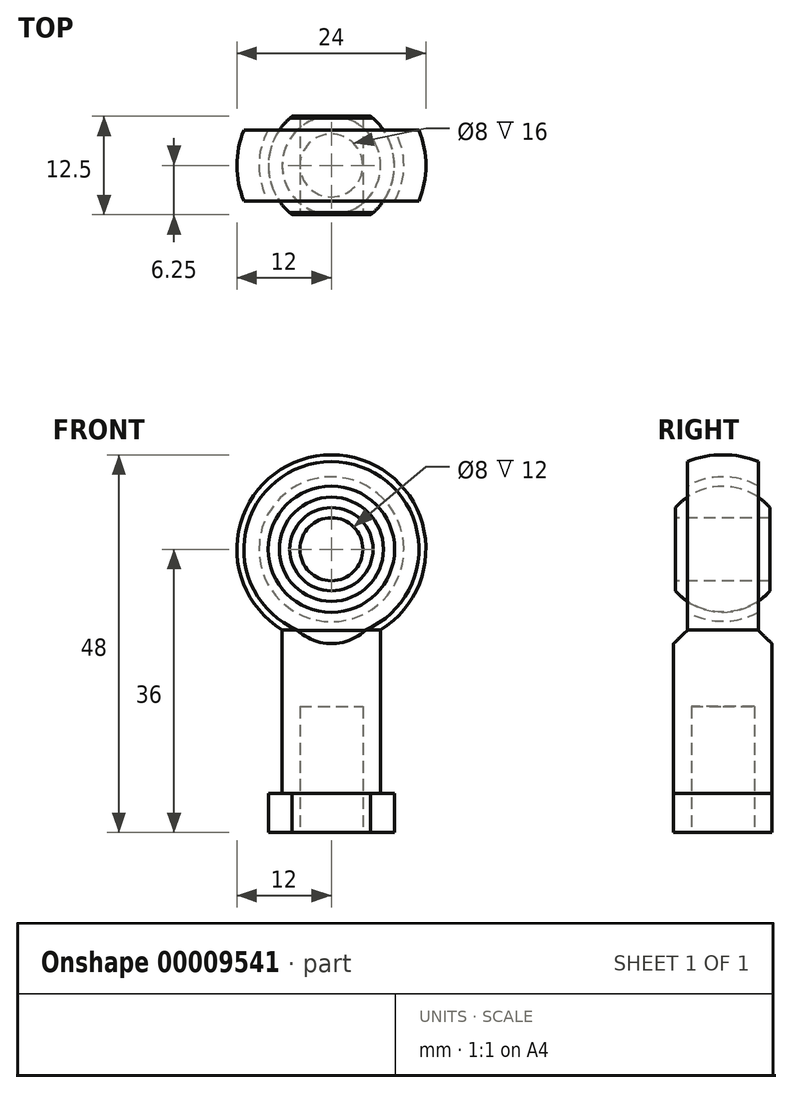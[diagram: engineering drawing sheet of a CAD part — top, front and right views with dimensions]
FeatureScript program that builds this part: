
annotation { "Feature Type Name" : "Feature", "Feature Type Description" : "" }
export const myFeature = defineFeature(function(context is Context, id is Id, definition is map)
    precondition{}
    {
        {
            var Q0;
            Q0=qCreatedBy(makeId("Front.planeOp"),FACE);
            var sketch = newSketch(context, id + "F0", { "sketchPlane" : qUnion([Q0])});
            skLineSegment(sketch, "E0", {"start": v(0, -62.5) * mm, "end": v(0, 62.8) * mm, "construction": true});
            skLineSegment(sketch, "E1", {"start": v(-34.6, 0) * mm, "end": v(39.27, 0) * mm, "construction": true});
            skLineSegment(sketch, "E2", {"start": v(0, -36) * mm, "end": v(6.25, -36) * mm});
            skCircle(sketch, "E3", {"center": v(0, 0) * mm, "radius": 12 * mm});
            skLineSegment(sketch, "E4", {"start": v(6.25, -36) * mm, "end": v(6.25, -10.24) * mm});
            skLineSegment(sketch, "E5.0", {"start": v(8, -36) * mm, "end": v(8, -31) * mm});
            skLineSegment(sketch, "E6", {"start": v(6.25, -36) * mm, "end": v(8, -36) * mm});
            skLineSegment(sketch, "E7.0", {"start": v(6.25, -31) * mm, "end": v(8, -31) * mm});
            skLineSegment(sketch, "E8", {"start": v(4, -36) * mm, "end": v(4, -20) * mm});
            skLineSegment(sketch, "E9", {"start": v(4, -20) * mm, "end": v(0, -20) * mm});
            skCircle(sketch, "E10", {"center": v(0, 0) * mm, "radius": 4 * mm});
            skCircle(sketch, "E11.0", {"center": v(0, 0) * mm, "radius": 6 * mm});
            skLineSegment(sketch, "E12", {"start": v(6.25, -10.24) * mm, "end": v(0, -10.24) * mm});
            skLineSegment(sketch, "E13", {"start": v(0, -10.24) * mm, "end": v(0, -20) * mm});
            skLineSegment(sketch, "E14.left", {"start": v(6.25, -36) * mm, "end": v(6.25, -31) * mm});
            skLineSegment(sketch, "E15.0.MirrorCS", {"start": v(-6.25, -31) * mm, "end": v(-8, -31) * mm});
            skLineSegment(sketch, "E16.0.MirrorCS", {"start": v(-8, -36) * mm, "end": v(-8, -31) * mm});
            skLineSegment(sketch, "E17.0.MirrorCS", {"start": v(-6.25, -36) * mm, "end": v(-6.25, -10.24) * mm});
            skLineSegment(sketch, "E18.0.MirrorCS", {"start": v(-6.25, -36) * mm, "end": v(-8, -36) * mm});
            skLineSegment(sketch, "E19.0.MirrorCS", {"start": v(-4, -36) * mm, "end": v(-4, -20) * mm});
            skLineSegment(sketch, "E20.0.MirrorCS", {"start": v(-4, -20) * mm, "end": v(0, -20) * mm});
            skLineSegment(sketch, "E21.0.MirrorCS", {"start": v(0, -36) * mm, "end": v(-6.25, -36) * mm});
            skSolve(sketch);
        }
        {
            var Q0;
            Q0=qCreatedBy(makeId("Right.planeOp"),FACE);
            var sketch = newSketch(context, id + "F1", { "sketchPlane" : qUnion([Q0])});
            skArc(sketch, "E22", {"start": v(4.5, 11.12) * mm, "mid": v(2.3, 11.78) * mm, "end": v(0, 12) * mm});
            skLineSegment(sketch, "E23", {"start": v(4.5, 11.12) * mm, "end": v(4.5, 6.61) * mm});
            skLineSegment(sketch, "E24.0", {"start": v(6, 5.3) * mm, "end": v(6, 4) * mm});
            skLineSegment(sketch, "E25", {"start": v(0, 4) * mm, "end": v(6, 4) * mm});
            skArc(sketch, "E26.trimOffspring", {"start": v(0, -12) * mm, "mid": v(2.3, -11.78) * mm, "end": v(4.5, -11.12) * mm});
            skLineSegment(sketch, "E27", {"start": v(-27.78, 0) * mm, "end": v(33.25, 0) * mm, "construction": true});
            skLineSegment(sketch, "E28.0", {"start": v(0, -4) * mm, "end": v(6, -4) * mm});
            skLineSegment(sketch, "E29.trimOffspring", {"start": v(4.5, -6.61) * mm, "end": v(4.5, -11.12) * mm});
            skLineSegment(sketch, "E30.trimOffspring", {"start": v(6, -4) * mm, "end": v(6, -5.3) * mm});
            skArc(sketch, "E31", {"start": v(6, 5.3) * mm, "mid": v(3.3, 7.3) * mm, "end": v(0, 8) * mm});
            skLineSegment(sketch, "E32", {"start": v(0, 30.57) * mm, "end": v(0, -12) * mm, "construction": true});
            skArc(sketch, "E33.trimOffspring", {"start": v(0, -8) * mm, "mid": v(3.3, -7.3) * mm, "end": v(6, -5.3) * mm});
            skArc(sketch, "E34", {"start": v(0, -9.2) * mm, "mid": v(2.33, -8.9) * mm, "end": v(4.5, -8.02) * mm});
            skArc(sketch, "E35.trimOffspring", {"start": v(4.5, 8.02) * mm, "mid": v(2.33, 8.9) * mm, "end": v(0, 9.2) * mm});
            skLineSegment(sketch, "E36.0.MirrorCS", {"start": v(-6, 5.3) * mm, "end": v(-6, 4) * mm});
            skLineSegment(sketch, "E36.1.MirrorCS", {"start": v(-6, -4) * mm, "end": v(-6, -5.3) * mm});
            skArc(sketch, "E36.2.MirrorCS", {"start": v(-4.5, 11.12) * mm, "mid": v(-2.3, 11.78) * mm, "end": v(0, 12) * mm});
            skLineSegment(sketch, "E36.3.MirrorCS", {"start": v(-4.5, 11.12) * mm, "end": v(-4.5, 6.61) * mm});
            skArc(sketch, "E36.4.MirrorCS", {"start": v(-4.5, 8.02) * mm, "mid": v(-2.33, 8.9) * mm, "end": v(0, 9.2) * mm});
            skLineSegment(sketch, "E36.5.MirrorCS", {"start": v(0, 4) * mm, "end": v(-6, 4) * mm});
            skArc(sketch, "E36.6.MirrorCS", {"start": v(0, -9.2) * mm, "mid": v(-2.33, -8.9) * mm, "end": v(-4.5, -8.02) * mm});
            skArc(sketch, "E36.7.MirrorCS", {"start": v(0, -12) * mm, "mid": v(-2.3, -11.78) * mm, "end": v(-4.5, -11.12) * mm});
            skArc(sketch, "E36.8.MirrorCS", {"start": v(-6, 5.3) * mm, "mid": v(-3.3, 7.3) * mm, "end": v(0, 8) * mm});
            skArc(sketch, "E36.9.MirrorCS", {"start": v(0, -8) * mm, "mid": v(-3.3, -7.3) * mm, "end": v(-6, -5.3) * mm});
            skLineSegment(sketch, "E36.10.MirrorCS", {"start": v(0, -4) * mm, "end": v(-6, -4) * mm});
            skLineSegment(sketch, "E36.11.MirrorCS", {"start": v(-4.5, -6.61) * mm, "end": v(-4.5, -11.12) * mm});
            skLineSegment(sketch, "E37", {"start": v(0, -10.3) * mm, "end": v(4.5, -10.3) * mm});
            skLineSegment(sketch, "E38", {"start": v(4.5, -10.3) * mm, "end": v(9, -14.63) * mm});
            skLineSegment(sketch, "E39", {"start": v(9, -14.63) * mm, "end": v(9, -9.57) * mm});
            skLineSegment(sketch, "E40", {"start": v(9, -9.57) * mm, "end": v(4.5, -9.57) * mm});
            skLineSegment(sketch, "E41", {"start": v(4.5, -9.57) * mm, "end": v(4.5, -10.3) * mm});
            skLineSegment(sketch, "E42", {"start": v(0, -10.3) * mm, "end": v(-4.5, -10.3) * mm});
            skLineSegment(sketch, "E43", {"start": v(-4.5, -10.3) * mm, "end": v(-9, -14.63) * mm});
            skLineSegment(sketch, "E44", {"start": v(-9, -14.63) * mm, "end": v(-9, -9.5) * mm});
            skLineSegment(sketch, "E45", {"start": v(-9, -9.5) * mm, "end": v(-4.5, -9.5) * mm});
            skLineSegment(sketch, "E46", {"start": v(6.25, -30.7) * mm, "end": v(10.17, -30.7) * mm});
            skLineSegment(sketch, "E47", {"start": v(10.17, -30.7) * mm, "end": v(10.17, -36.6) * mm});
            skLineSegment(sketch, "E48", {"start": v(10.17, -36.6) * mm, "end": v(6.25, -36.6) * mm});
            skLineSegment(sketch, "E49.0", {"start": v(6.25, -36.6) * mm, "end": v(6.25, -30.7) * mm});
            skPoint(sketch, "E50.start.orphan", {"position": v(0, -36.6) * mm});
            skLineSegment(sketch, "E51.trimOffspring", {"start": v(0, -36.6) * mm, "end": v(0, -83.02) * mm, "construction": true});
            skLineSegment(sketch, "E52.0.MirrorCS", {"start": v(-6.25, -36.6) * mm, "end": v(-6.25, -30.7) * mm});
            skLineSegment(sketch, "E52.1.MirrorCS", {"start": v(-6.25, -30.7) * mm, "end": v(-10.17, -30.7) * mm});
            skLineSegment(sketch, "E52.2.MirrorCS", {"start": v(-10.17, -30.7) * mm, "end": v(-10.17, -36.6) * mm});
            skLineSegment(sketch, "E52.3.MirrorCS", {"start": v(-10.17, -36.6) * mm, "end": v(-6.25, -36.6) * mm});
            skSolve(sketch);
        }
        {
            var Q0;
            {var subQ5=sQuery(id+"F1.wireOp",EDGE,"E22");Q0=makeQuery(id+"F1.imprint","IMPRINT",FACE,{"disambiguationData":[TD([[makeQuery(id+"F1.imprint","IMPRINT",EDGE,{"derivedFrom":subQ5}),1.0]])]});}
            var Q1;
            Q1=sQuery(id+"F1.wireOp",EDGE,"E27");
            revolve(context, id + "F2", {"entities" : qUnion([Q0]), "axis" : qUnion([Q1]), "revolveType" : RevolveType.FULL});
        }
        {
            var Q0;
            {var subQ5=sQuery(id+"F1.wireOp",EDGE,"E24.0");Q0=makeQuery(id+"F1.imprint","IMPRINT",FACE,{"disambiguationData":[TD([[makeQuery(id+"F1.imprint","IMPRINT",EDGE,{"derivedFrom":subQ5}),-1.0]])]});}
            var Q1;
            Q1=sQuery(id+"F1.wireOp",EDGE,"E27");
            revolve(context, id + "F3", {"entities" : qUnion([Q0]), "axis" : qUnion([Q1]), "revolveType" : RevolveType.FULL});
        }
        {
            var Q0;
            {var subQ6=sQuery(id+"F1.wireOp",EDGE,"E35.trimOffspring");Q0=makeQuery(id+"F1.imprint","IMPRINT",FACE,{"disambiguationData":[TD([[makeQuery(id+"F1.imprint","IMPRINT",EDGE,{"derivedFrom":subQ6}),1.0]])]});}
            var Q1;
            Q1=sQuery(id+"F1.wireOp",EDGE,"E27");
            revolve(context, id + "F4", {"entities" : qUnion([Q0]), "axis" : qUnion([Q1]), "revolveType" : RevolveType.FULL});
        }
        {
            var Q0;
            {var subQ4=sQuery(id+"F0.wireOp",EDGE,"E8");Q0=makeQuery(id+"F0.imprint","IMPRINT",FACE,{"disambiguationData":[TD([[makeQuery(id+"F0.imprint","IMPRINT",EDGE,{"derivedFrom":subQ4}),-1.0]])]});}
            var Q1;
            {var subQ3=sQuery(id+"F0.wireOp",EDGE,"E12");Q1=makeQuery(id+"F0.imprint","IMPRINT",FACE,{"disambiguationData":[TD([[makeQuery(id+"F0.imprint","IMPRINT",EDGE,{"derivedFrom":subQ3}),1.0]])]});}
            var Q2;
            Q2=makeQuery(id+"F0.imprint","IMPRINT",FACE,{"disambiguationData":[TD([[makeQuery(id+"F0.imprint","IMPRINT",EDGE,{"derivedFrom":sQuery(id+"F0.wireOp",EDGE,"E5.0")}),1.0]])]});
            var Q3;
            Q3=sQuery(id+"F0.wireOp",EDGE,"E0");
            revolve(context, id + "F5", {"operationType" : NewBodyOperationType.ADD, "entities" : qUnion([Q0, Q1, Q2]), "axis" : qUnion([Q3]), "revolveType" : RevolveType.FULL});
        }
        {
            var Q0;
            Q0=makeQuery(id+"F1.imprint","IMPRINT",FACE,{"disambiguationData":[TD([[makeQuery(id+"F1.imprint","IMPRINT",EDGE,{"derivedFrom":sQuery(id+"F1.wireOp",EDGE,"E38")}),1.0]])]});
            var Q1;
            {var subQ1=sQuery(id+"F1.wireOp",EDGE,"E43");Q1=makeQuery(id+"F1.imprint","IMPRINT",FACE,{"disambiguationData":[TD([[makeQuery(id+"F1.imprint","IMPRINT",EDGE,{"derivedFrom":subQ1}),-1.0]])]});}
            extrude(context, id + "F6", {"entities" : qUnion([Q0, Q1]), "operationType" : NewBodyOperationType.REMOVE, "depth" : 10 * mm, "hasSecondDirection" : true, "secondDirectionOppositeDirection" : true, "secondDirectionDepth" : 10 * mm});
        }
        {
            var Q0;
            Q0=makeQuery(id+"F0.imprint","IMPRINT",FACE,{"disambiguationData":[TD([[makeQuery(id+"F0.imprint","IMPRINT",EDGE,{"derivedFrom":sQuery(id+"F0.wireOp",EDGE,"E6")}),1.0]])]});
            var Q1;
            Q1=makeQuery(id+"F5.opRevolve","SWEPT_FACE",FACE,{"disambiguationData":[OSD([sQuery(id+"F0.wireOp",EDGE,"E4"),sQuery(id+"F0.wireOp",EDGE,"E14.left")])]});
            revolve(context, id + "F7", {"operationType" : NewBodyOperationType.ADD, "entities" : qUnion([Q0]), "axis" : qUnion([Q1]), "revolveType" : RevolveType.FULL});
        }
        {
            var Q0;
            Q0=makeQuery(id+"F1.imprint","IMPRINT",FACE,{"disambiguationData":[TD([[makeQuery(id+"F1.imprint","IMPRINT",EDGE,{"derivedFrom":sQuery(id+"F1.wireOp",EDGE,"E52.0.MirrorCS")}),1.0]])]});
            var Q1;
            Q1=makeQuery(id+"F1.imprint","IMPRINT",FACE,{"disambiguationData":[TD([[makeQuery(id+"F1.imprint","IMPRINT",EDGE,{"derivedFrom":sQuery(id+"F1.wireOp",EDGE,"E46")}),-1.0]])]});
            extrude(context, id + "F8", {"entities" : qUnion([Q0, Q1]), "operationType" : NewBodyOperationType.REMOVE, "oppositeDirection" : true, "depth" : 10 * mm, "hasSecondDirection" : true, "secondDirectionOppositeDirection" : false, "secondDirectionDepth" : 10000 * mm});
        }
    });
